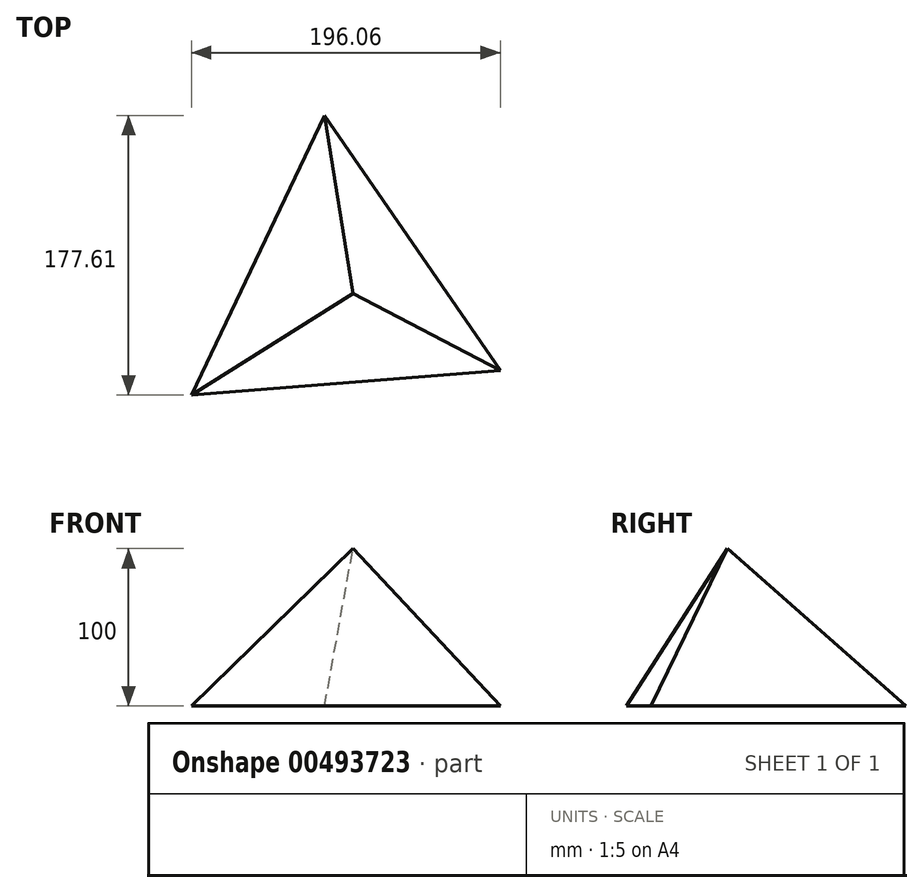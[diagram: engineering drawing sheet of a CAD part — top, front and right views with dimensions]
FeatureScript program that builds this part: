
annotation { "Feature Type Name" : "Feature", "Feature Type Description" : "" }
export const myFeature = defineFeature(function(context is Context, id is Id, definition is map)
    precondition{}
    {
        {
            var Q0;
            Q0=qCreatedBy(makeId("Top.planeOp"),FACE);
            var sketch = newSketch(context, id + "F0", { "sketchPlane" : qUnion([Q0])});
            skCircle(sketch, "E0.cCircle", {"center": v(0, 0) * mm, "radius": 113.56 * mm, "construction": true});
            skLineSegment(sketch, "E0.0", {"start": v(-93.52, -64.4) * mm, "end": v(-9.01, 113.2) * mm});
            skLineSegment(sketch, "E0.1", {"start": v(-9.01, 113.2) * mm, "end": v(102.54, -48.8) * mm});
            skLineSegment(sketch, "E0.2", {"start": v(102.54, -48.8) * mm, "end": v(-93.52, -64.4) * mm});
            skSolve(sketch);
        }
        {
            var Q0;
            Q0=qCreatedBy(makeId("Top.planeOp"),FACE);
            cPlane(context, id + "F1", {"entities" : qUnion([Q0]), "cplaneType" : CPlaneType.OFFSET, "offset" : 100 * mm, "width" : 150 * mm, "height" : 150 * mm});
        }
        {
            var Q0;
            Q0=qCreatedBy(id+"F1.planeOp",FACE);
            var sketch = newSketch(context, id + "F2", { "sketchPlane" : qUnion([Q0])});
            skPoint(sketch, "E1", {"position": v(9.02, 0) * mm});
            skSolve(sketch);
        }
        {
            var Q0;
            Q0=makeQuery(id+"F0.imprint","IMPRINT",FACE,{"disambiguationData":[TD([[makeQuery(id+"F0.imprint","IMPRINT",EDGE,{"derivedFrom":sQuery(id+"F0.wireOp",EDGE,"E0.0")}),-1.0]])]});
            var Q1;
            Q1=sQuery(id+"F2.wireOp",VERTEX,"E1");
            loft(context, id + "F3", {"sheetProfilesArray" : [{ "sheetProfileEntities" : qUnion([Q0]) }, { "sheetProfileEntities" : qUnion([Q1]) }]});
        }
    });
